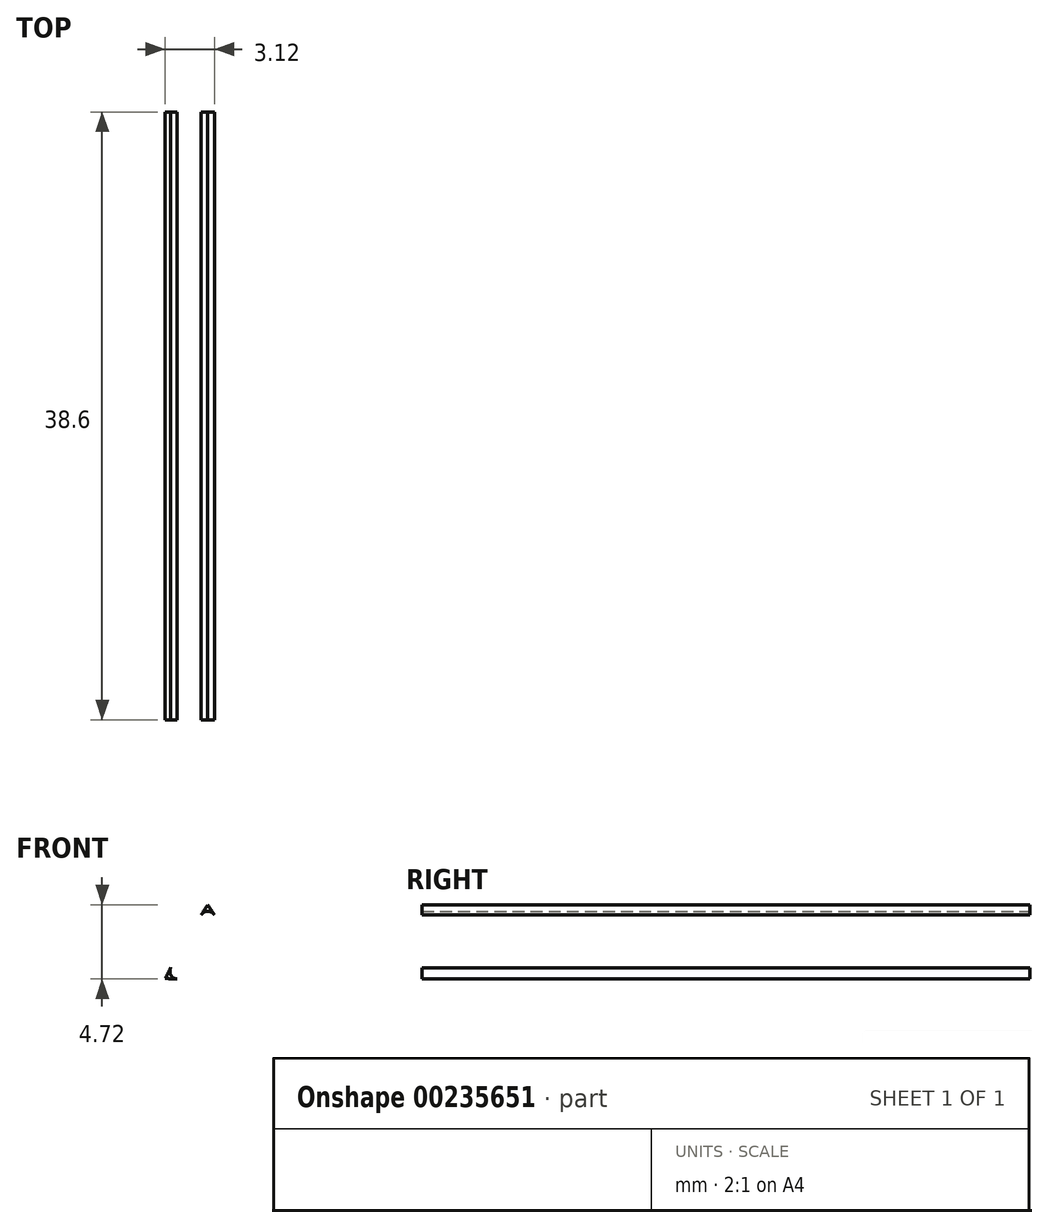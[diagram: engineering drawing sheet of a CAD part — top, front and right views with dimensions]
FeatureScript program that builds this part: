
annotation { "Feature Type Name" : "Feature", "Feature Type Description" : "" }
export const myFeature = defineFeature(function(context is Context, id is Id, definition is map)
    precondition{}
    {
        {
            var Q0;
            Q0=qCreatedBy(makeId("Front.planeOp"),FACE);
            var sketch = newSketch(context, id + "F0", { "sketchPlane" : qUnion([Q0])});
            skFitSpline(sketch, "E0", {"points": [v(0, 0) * mm, v(1.26, 2.39) * mm, v(2.7, 4.68) * mm], "startDerivative": vector(2.44, 4.83) * mm, "endDerivative": vector(2.96, 4.53) * mm});
            skFitSpline(sketch, "E1", {"points": [v(2.7, 4.68) * mm, v(4.14, 2.39) * mm, v(5.4, 0) * mm], "startDerivative": vector(2.96, -4.53) * mm, "endDerivative": vector(2.44, -4.83) * mm});
            skFitSpline(sketch, "E2", {"points": [v(5.4, 0) * mm, v(2.7, -0.1) * mm, v(0, 0) * mm], "startDerivative": vector(-5.4, -0.3) * mm, "endDerivative": vector(-5.4, 0.3) * mm});
            skArc(sketch, "E3.filletArc", {"start": v(3.12, 4.03) * mm, "mid": v(2.7, 4.26) * mm, "end": v(2.28, 4.03) * mm});
            skArc(sketch, "E4.filletArc", {"start": v(4.63, -0.04) * mm, "mid": v(5.04, 0.2) * mm, "end": v(5.05, 0.69) * mm});
            skArc(sketch, "E5.filletArc", {"start": v(0.35, 0.69) * mm, "mid": v(0.36, 0.2) * mm, "end": v(0.77, -0.04) * mm});
            skSolve(sketch);
        }
        {
            var Q0;
            Q0=makeQuery(id+"F0.imprint","IMPRINT",FACE,{"disambiguationData":[TD([[makeQuery(id+"F0.imprint","IMPRINT",EDGE,{"derivedFrom":sQuery(id+"F0.wireOp",EDGE,"E0")}),-1.0]])]});
            extrude(context, id + "F1", {"entities" : qUnion([Q0]), "depth" : 38.6 * mm});
        }
    });
